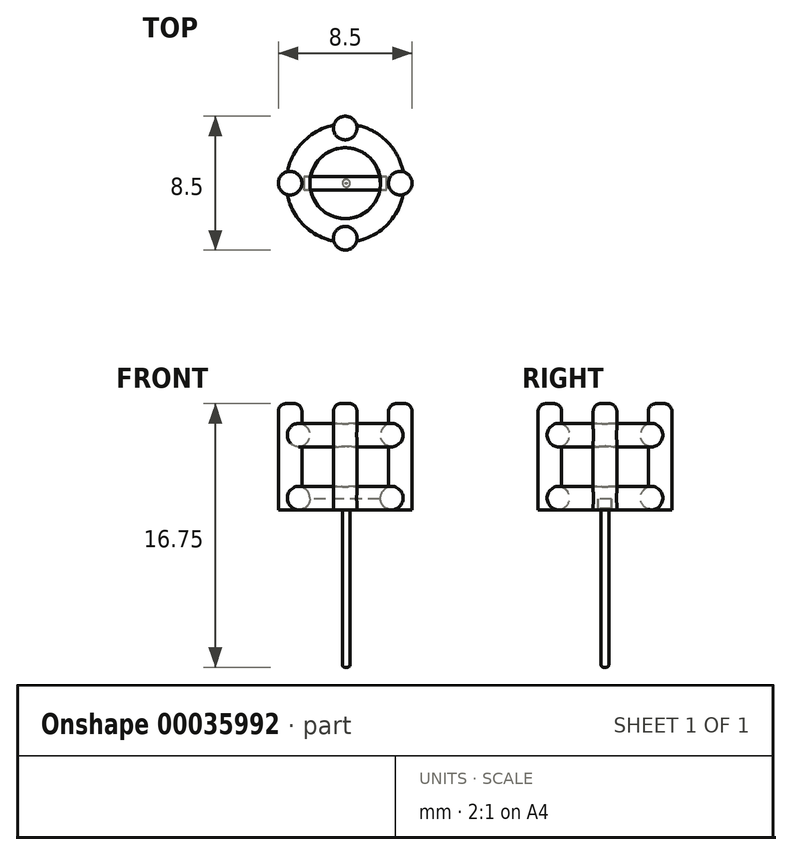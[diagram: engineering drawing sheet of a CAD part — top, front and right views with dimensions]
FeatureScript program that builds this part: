
annotation { "Feature Type Name" : "Feature", "Feature Type Description" : "" }
export const myFeature = defineFeature(function(context is Context, id is Id, definition is map)
    precondition{}
    {
        {
            var Q0;
            Q0=qCreatedBy(makeId("Front.planeOp"),FACE);
            var sketch = newSketch(context, id + "F0", { "sketchPlane" : qUnion([Q0])});
            skCircle(sketch, "E0", {"center": v(3, 0) * mm, "radius": 0.75 * mm});
            skCircle(sketch, "E1", {"center": v(3, 4) * mm, "radius": 0.75 * mm});
            skLineSegment(sketch, "E2", {"start": v(0, 7.34) * mm, "end": v(0, -9.86) * mm, "construction": true});
            skSolve(sketch);
        }
        {
            var Q0;
            Q0 = qSketchRegion(id + "F0", true);
            var Q1;
            Q1=sQuery(id+"F0.wireOp",EDGE,"E2");
            revolve(context, id + "F1", {"entities" : qUnion([Q0]), "axis" : qUnion([Q1]), "revolveType" : RevolveType.FULL});
        }
        {
            var Q0;
            Q0=qCreatedBy(makeId("Right.planeOp"),FACE);
            var sketch = newSketch(context, id + "F2", { "sketchPlane" : qUnion([Q0])});
            skLineSegment(sketch, "E3", {"start": v(0, 11.43) * mm, "end": v(0, -8.77) * mm, "construction": true});
            skSolve(sketch);
        }
        {
            var Q0;
            Q0=qCreatedBy(makeId("Top.planeOp"),FACE);
            var sketch = newSketch(context, id + "F3", { "sketchPlane" : qUnion([Q0])});
            skCircle(sketch, "E4", {"center": v(3.5, 0) * mm, "radius": 0.75 * mm});
            skSolve(sketch);
        }
        {
            var Q0;
            Q0 = qSketchRegion(id + "F3", true);
            extrude(context, id + "F4", {"entities" : qUnion([Q0]), "depth" : 6 * mm, "hasSecondDirection" : true, "secondDirectionOppositeDirection" : true, "secondDirectionDepth" : .75 * mm});
        }
        {
            var Q0;
            Q0=makeQuery(id+"F4.opExtrude","SWEPT_BODY",BODY,{"disambiguationData":[OSD([sQuery(id+"F3.wireOp",EDGE,"E4")])]});
            var Q1;
            Q1=sQuery(id+"F2.wireOp",EDGE,"E3");
            circularPattern(context, id + "F5", {"operationType" : NewBodyOperationType.ADD, "entities" : qUnion([Q0]), "axis" : qUnion([Q1]), "angle" : 360 * degree, "instanceCount" : 4, "equalSpace" : true});
        }
        {
            var Q0;
            Q0=makeQuery(id+"F4.opExtrude","CAP_EDGE",EDGE,{"disambiguationData":[OSD([sQuery(id+"F3.wireOp",EDGE,"E4")])],"isStart":false});
            var Q1;
            Q1=makeQuery(id+"F5.opPattern","COPY",EDGE,{"derivedFrom":makeQuery(id+"F4.opExtrude","CAP_EDGE",EDGE,{"disambiguationData":[OSD([sQuery(id+"F3.wireOp",EDGE,"E4")])],"isStart":false}),"instanceName":"1"});
            var Q2;
            Q2=makeQuery(id+"F5.opPattern","COPY",EDGE,{"derivedFrom":makeQuery(id+"F4.opExtrude","CAP_EDGE",EDGE,{"disambiguationData":[OSD([sQuery(id+"F3.wireOp",EDGE,"E4")])],"isStart":false}),"instanceName":"2"});
            var Q3;
            Q3=makeQuery(id+"F5.opPattern","COPY",EDGE,{"derivedFrom":makeQuery(id+"F4.opExtrude","CAP_EDGE",EDGE,{"disambiguationData":[OSD([sQuery(id+"F3.wireOp",EDGE,"E4")])],"isStart":false}),"instanceName":"3"});
            fillet(context, id + "F6", {"entities" : qUnion([Q0, Q1, Q2, Q3]), "radius" : .5 * mm, "tangentPropagation" : true, "allowEdgeOverflow" : false});
        }
        {
            var Q0;
            Q0=makeQuery(id+"F5.opPattern","COPY",FACE,{"derivedFrom":makeQuery(id+"F4.opExtrude","CAP_FACE",FACE,{"disambiguationData":[OSD([sQuery(id+"F3.wireOp",EDGE,"E4")])],"isStart":true}),"instanceName":"2"});
            var sketch = newSketch(context, id + "F7", { "sketchPlane" : qUnion([Q0])});
            skLineSegment(sketch, "E5.rect.bottom", {"start": v(2.63, 0.44) * mm, "end": v(-2.62, 0.44) * mm});
            skLineSegment(sketch, "E5.rect.top", {"start": v(2.63, -0.42) * mm, "end": v(-2.62, -0.42) * mm});
            skLineSegment(sketch, "E5.rect.left", {"start": v(2.63, 0.44) * mm, "end": v(2.63, -0.42) * mm});
            skLineSegment(sketch, "E5.rect.right", {"start": v(-2.62, 0.44) * mm, "end": v(-2.62, -0.42) * mm});
            skPoint(sketch, "E5.rect.middle", {"position": v(0, 0) * mm});
            skSolve(sketch);
        }
        {
            var Q0;
            Q0 = qSketchRegion(id + "F7", true);
            extrude(context, id + "F8", {"entities" : qUnion([Q0]), "operationType" : NewBodyOperationType.ADD, "oppositeDirection" : true, "depth" : 0.7 * mm});
        }
        {
            var Q0;
            Q0=makeQuery(id+"F8.opExtrude","CAP_FACE",FACE,{"disambiguationData":[OSD([sQuery(id+"F7.wireOp",EDGE,"E5.rect.bottom"),sQuery(id+"F7.wireOp",EDGE,"E5.rect.top"),sQuery(id+"F7.wireOp",EDGE,"E5.rect.left"),sQuery(id+"F7.wireOp",EDGE,"E5.rect.right")])],"isStart":true});
            var sketch = newSketch(context, id + "F9", { "sketchPlane" : qUnion([Q0])});
            skCircle(sketch, "E6", {"center": v(0.06, 0) * mm, "radius": 0.25 * mm});
            skSolve(sketch);
        }
        {
            var Q0;
            Q0 = qSketchRegion(id + "F9", true);
            extrude(context, id + "F10", {"entities" : qUnion([Q0]), "operationType" : NewBodyOperationType.ADD, "depth" : (10) * mm});
        }
        {
            var Q0;
            Q0=makeQuery(id+"F10.opExtrude","CAP_FACE",FACE,{"disambiguationData":[OSD([sQuery(id+"F9.wireOp",EDGE,"E6")])],"isStart":false});
            fillet(context, id + "F11", {"entities" : qUnion([Q0]), "radius" : 0.2 * mm, "tangentPropagation" : true, "rho" : 0.5, "crossSection" : FilletCrossSection.CONIC, "allowEdgeOverflow" : false});
        }
    });
